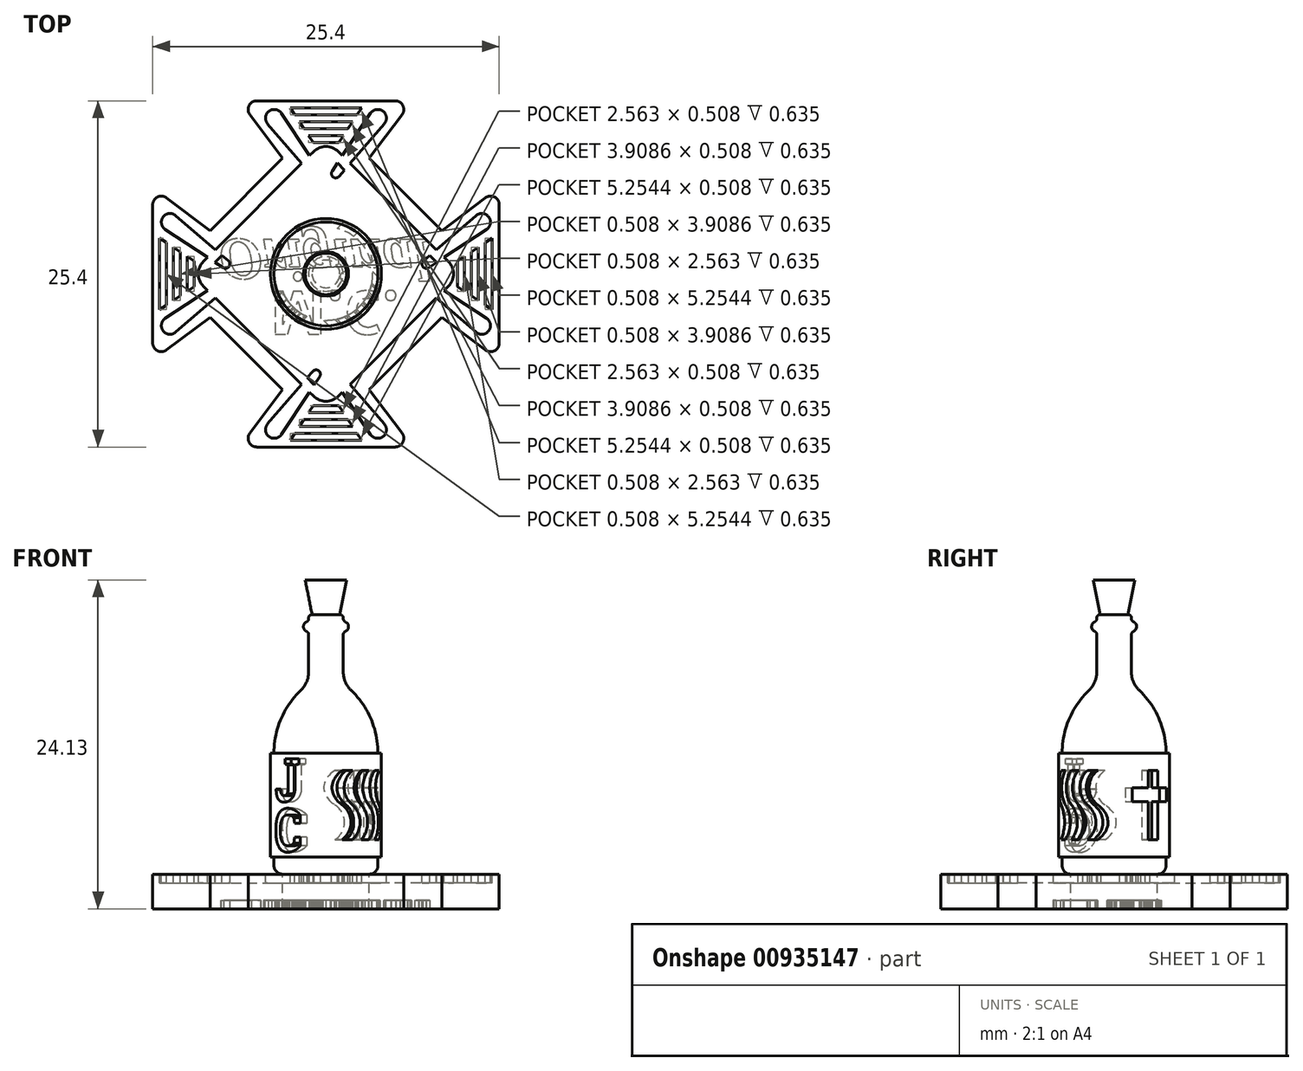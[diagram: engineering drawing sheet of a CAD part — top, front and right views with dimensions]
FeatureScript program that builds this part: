
annotation { "Feature Type Name" : "Feature", "Feature Type Description" : "" }
export const myFeature = defineFeature(function(context is Context, id is Id, definition is map)
    precondition{}
    {
        {
            var Q0;
            Q0=qCreatedBy(makeId("Top.planeOp"),FACE);
            var sketch = newSketch(context, id + "F0", { "sketchPlane" : qUnion([Q0])});
            skLineSegment(sketch, "E0", {"start": v(0, 24.37) * mm, "end": v(0, -22.03) * mm, "construction": true});
            skLineSegment(sketch, "E1", {"start": v(-24.6, 0) * mm, "end": v(22.72, 0) * mm, "construction": true});
            skLineSegment(sketch, "E2", {"start": v(0, 11.67) * mm, "end": v(-11.67, 0) * mm});
            skLineSegment(sketch, "E3.MirrorCS", {"start": v(0, 11.67) * mm, "end": v(11.67, 0) * mm});
            skLineSegment(sketch, "E4.MirrorCS", {"start": v(0, -11.67) * mm, "end": v(-11.67, 0) * mm});
            skLineSegment(sketch, "E5.MirrorCS", {"start": v(0, -11.67) * mm, "end": v(11.67, 0) * mm});
            skLineSegment(sketch, "E6", {"start": v(0, 12.7) * mm, "end": v(-6.35, 12.7) * mm});
            skLineSegment(sketch, "E7", {"start": v(-6.35, 12.7) * mm, "end": v(-3.17, 8.5) * mm});
            skPoint(sketch, "E7.endSnap0", {"position": v(-3.17, 12.7) * mm});
            skLineSegment(sketch, "E8.MirrorCS", {"start": v(0, 12.7) * mm, "end": v(6.35, 12.7) * mm});
            skLineSegment(sketch, "E9.MirrorCS", {"start": v(6.35, 12.7) * mm, "end": v(3.17, 8.5) * mm});
            skLineSegment(sketch, "E10.MirrorCS", {"start": v(6.35, -12.7) * mm, "end": v(3.17, -8.5) * mm});
            skLineSegment(sketch, "E11.MirrorCS", {"start": v(0, -12.7) * mm, "end": v(6.35, -12.7) * mm});
            skLineSegment(sketch, "E12.MirrorCS", {"start": v(0, -12.7) * mm, "end": v(-6.35, -12.7) * mm});
            skLineSegment(sketch, "E13.MirrorCS", {"start": v(-6.35, -12.7) * mm, "end": v(-3.17, -8.5) * mm});
            skLineSegment(sketch, "E14", {"start": v(0, 0) * mm, "end": v(5.84, -5.84) * mm, "construction": true});
            skLineSegment(sketch, "E15.MirrorCS", {"start": v(12.7, -6.35) * mm, "end": v(8.5, -3.18) * mm});
            skLineSegment(sketch, "E16.MirrorCS", {"start": v(12.7, 0) * mm, "end": v(12.7, -6.35) * mm});
            skLineSegment(sketch, "E17.MirrorCS", {"start": v(12.7, 0) * mm, "end": v(12.7, 6.35) * mm});
            skLineSegment(sketch, "E18.MirrorCS", {"start": v(12.7, 6.35) * mm, "end": v(8.5, 3.17) * mm});
            skLineSegment(sketch, "E19.MirrorCS", {"start": v(-12.7, 6.35) * mm, "end": v(-8.5, 3.17) * mm});
            skLineSegment(sketch, "E20.MirrorCS", {"start": v(-12.7, 0) * mm, "end": v(-12.7, 6.35) * mm});
            skLineSegment(sketch, "E21.MirrorCS", {"start": v(-12.7, 0) * mm, "end": v(-12.7, -6.35) * mm});
            skLineSegment(sketch, "E22.MirrorCS", {"start": v(-12.7, -6.35) * mm, "end": v(-8.5, -3.18) * mm});
            skSolve(sketch);
        }
        {
            var Q0;
            Q0=qSketchRegion(id+"F0",true);
            extrude(context, id + "F1", {"entities" : qUnion([Q0]), "oppositeDirection" : true, "depth" : 2.54 * mm, "offsetDistance" : 25.4 * mm});
        }
        {
            var Q0;
            Q0=makeQuery(id+"F1.opExtrude","SWEPT_EDGE",EDGE,{"disambiguationData":[OSD([sQuery(id+"F0.wireOp",EDGE,"E6"),sQuery(id+"F0.wireOp",EDGE,"E7")])]});
            var Q1;
            Q1=makeQuery(id+"F1.opExtrude","SWEPT_EDGE",EDGE,{"disambiguationData":[OSD([sQuery(id+"F0.wireOp",EDGE,"E19.MirrorCS"),sQuery(id+"F0.wireOp",EDGE,"E20.MirrorCS")])]});
            var Q2;
            Q2=makeQuery(id+"F1.opExtrude","SWEPT_EDGE",EDGE,{"disambiguationData":[OSD([sQuery(id+"F0.wireOp",EDGE,"E8.MirrorCS"),sQuery(id+"F0.wireOp",EDGE,"E9.MirrorCS")])]});
            var Q3;
            Q3=makeQuery(id+"F1.opExtrude","SWEPT_EDGE",EDGE,{"disambiguationData":[OSD([sQuery(id+"F0.wireOp",EDGE,"E17.MirrorCS"),sQuery(id+"F0.wireOp",EDGE,"E18.MirrorCS")])]});
            var Q4;
            Q4=makeQuery(id+"F1.opExtrude","SWEPT_EDGE",EDGE,{"disambiguationData":[OSD([sQuery(id+"F0.wireOp",EDGE,"E12.MirrorCS"),sQuery(id+"F0.wireOp",EDGE,"E13.MirrorCS")])]});
            var Q5;
            Q5=makeQuery(id+"F1.opExtrude","SWEPT_EDGE",EDGE,{"disambiguationData":[OSD([sQuery(id+"F0.wireOp",EDGE,"E21.MirrorCS"),sQuery(id+"F0.wireOp",EDGE,"E22.MirrorCS")])]});
            var Q6;
            Q6=makeQuery(id+"F1.opExtrude","SWEPT_EDGE",EDGE,{"disambiguationData":[OSD([sQuery(id+"F0.wireOp",EDGE,"E10.MirrorCS"),sQuery(id+"F0.wireOp",EDGE,"E11.MirrorCS")])]});
            var Q7;
            Q7=makeQuery(id+"F1.opExtrude","SWEPT_EDGE",EDGE,{"disambiguationData":[OSD([sQuery(id+"F0.wireOp",EDGE,"E15.MirrorCS"),sQuery(id+"F0.wireOp",EDGE,"E16.MirrorCS")])]});
            fillet(context, id + "F2", {"entities" : qUnion([Q0, Q1, Q2, Q3, Q4, Q5, Q6, Q7]), "radius" : 0.64 * mm, "tangentPropagation" : true, "allowEdgeOverflow" : false});
        }
        {
            var Q0;
            Q0=makeQuery(id+"F1.opExtrude","CAP_FACE",FACE,{"disambiguationData":[OSD([sQuery(id+"F0.wireOp",EDGE,"E2"),sQuery(id+"F0.wireOp",EDGE,"E3.MirrorCS"),sQuery(id+"F0.wireOp",EDGE,"E4.MirrorCS"),sQuery(id+"F0.wireOp",EDGE,"E5.MirrorCS"),sQuery(id+"F0.wireOp",EDGE,"E6"),sQuery(id+"F0.wireOp",EDGE,"E7"),sQuery(id+"F0.wireOp",EDGE,"E8.MirrorCS"),sQuery(id+"F0.wireOp",EDGE,"E9.MirrorCS"),sQuery(id+"F0.wireOp",EDGE,"E10.MirrorCS"),sQuery(id+"F0.wireOp",EDGE,"E11.MirrorCS"),sQuery(id+"F0.wireOp",EDGE,"E12.MirrorCS"),sQuery(id+"F0.wireOp",EDGE,"E13.MirrorCS"),sQuery(id+"F0.wireOp",EDGE,"E15.MirrorCS"),sQuery(id+"F0.wireOp",EDGE,"E16.MirrorCS"),sQuery(id+"F0.wireOp",EDGE,"E17.MirrorCS"),sQuery(id+"F0.wireOp",EDGE,"E18.MirrorCS"),sQuery(id+"F0.wireOp",EDGE,"E19.MirrorCS"),sQuery(id+"F0.wireOp",EDGE,"E20.MirrorCS"),sQuery(id+"F0.wireOp",EDGE,"E21.MirrorCS"),sQuery(id+"F0.wireOp",EDGE,"E22.MirrorCS")])],"isStart":true});
            var sketch = newSketch(context, id + "F3", { "sketchPlane" : qUnion([Q0])});
            skLineSegment(sketch, "E23", {"start": v(0, 16.4) * mm, "end": v(0, -16.14) * mm, "construction": true});
            skLineSegment(sketch, "E24", {"start": v(-8.98, 0.9) * mm, "end": v(-0.9, 8.98) * mm});
            skArc(sketch, "E25", {"start": v(0, 9.35) * mm, "mid": v(-0.49, 9.26) * mm, "end": v(-0.9, 8.98) * mm});
            skLineSegment(sketch, "E26", {"start": v(0, 0) * mm, "end": v(-13.8, 0) * mm, "construction": true});
            skLineSegment(sketch, "E27", {"start": v(0, 0) * mm, "end": v(-5.84, 5.84) * mm, "construction": true});
            skArc(sketch, "E28.MirrorCS", {"start": v(-9.35, 0) * mm, "mid": v(-9.26, 0.49) * mm, "end": v(-8.98, 0.9) * mm});
            skPoint(sketch, "E29.start.orphan", {"position": v(-9.88, 0) * mm});
            skArc(sketch, "E30.MirrorCS", {"start": v(-9.35, 0) * mm, "mid": v(-9.26, -0.49) * mm, "end": v(-8.98, -0.9) * mm});
            skLineSegment(sketch, "E31.MirrorCS", {"start": v(-8.98, -0.9) * mm, "end": v(-0.9, -8.98) * mm});
            skArc(sketch, "E32.MirrorCS", {"start": v(0, -9.35) * mm, "mid": v(-0.49, -9.26) * mm, "end": v(-0.9, -8.98) * mm});
            skArc(sketch, "E33.MirrorCS", {"start": v(0, 9.35) * mm, "mid": v(0.49, 9.26) * mm, "end": v(0.9, 8.98) * mm});
            skLineSegment(sketch, "E34.MirrorCS", {"start": v(8.98, 0.9) * mm, "end": v(0.9, 8.98) * mm});
            skArc(sketch, "E35.MirrorCS", {"start": v(9.35, 0) * mm, "mid": v(9.26, 0.49) * mm, "end": v(8.98, 0.9) * mm});
            skArc(sketch, "E36.MirrorCS", {"start": v(9.35, 0) * mm, "mid": v(9.26, -0.49) * mm, "end": v(8.98, -0.9) * mm});
            skLineSegment(sketch, "E37.MirrorCS", {"start": v(8.98, -0.9) * mm, "end": v(0.9, -8.98) * mm});
            skArc(sketch, "E38.MirrorCS", {"start": v(0, -9.35) * mm, "mid": v(0.49, -9.26) * mm, "end": v(0.9, -8.98) * mm});
            skLineSegment(sketch, "E39", {"start": v(-2.75, 10.05) * mm, "end": v(2.55, 3.03) * mm, "construction": true});
            skArc(sketch, "E40", {"start": v(-4.18, 11.94) * mm, "mid": v(-4.43, 11.5) * mm, "end": v(-4.28, 11.02) * mm});
            skArc(sketch, "E41", {"start": v(-0.96, 7.15) * mm, "mid": v(-0.76, 7.04) * mm, "end": v(-0.53, 7.1) * mm});
            skLineSegment(sketch, "E42", {"start": v(-4.28, 11.02) * mm, "end": v(-0.96, 7.15) * mm});
            skArc(sketch, "E43.MirrorCS", {"start": v(-0.46, 7.54) * mm, "mid": v(-0.4, 7.3) * mm, "end": v(-0.53, 7.1) * mm});
            skLineSegment(sketch, "E44.MirrorCS", {"start": v(-3.27, 11.78) * mm, "end": v(-0.46, 7.54) * mm});
            skArc(sketch, "E45.MirrorCS", {"start": v(-4.18, 11.94) * mm, "mid": v(-3.7, 12.06) * mm, "end": v(-3.27, 11.78) * mm});
            skArc(sketch, "E46.MirrorCS", {"start": v(4.18, 11.94) * mm, "mid": v(3.7, 12.06) * mm, "end": v(3.27, 11.78) * mm});
            skArc(sketch, "E47.MirrorCS", {"start": v(4.18, 11.94) * mm, "mid": v(4.43, 11.5) * mm, "end": v(4.28, 11.02) * mm});
            skLineSegment(sketch, "E48.MirrorCS", {"start": v(4.28, 11.02) * mm, "end": v(0.96, 7.15) * mm});
            skLineSegment(sketch, "E49.MirrorCS", {"start": v(3.27, 11.78) * mm, "end": v(0.46, 7.54) * mm});
            skArc(sketch, "E50.MirrorCS", {"start": v(0.96, 7.15) * mm, "mid": v(0.76, 7.04) * mm, "end": v(0.53, 7.1) * mm});
            skArc(sketch, "E51.MirrorCS", {"start": v(0.46, 7.54) * mm, "mid": v(0.4, 7.3) * mm, "end": v(0.53, 7.1) * mm});
            skArc(sketch, "E52.MirrorCS", {"start": v(-11.94, 4.18) * mm, "mid": v(-11.5, 4.43) * mm, "end": v(-11.02, 4.28) * mm});
            skArc(sketch, "E53.MirrorCS", {"start": v(-11.94, 4.18) * mm, "mid": v(-12.06, 3.7) * mm, "end": v(-11.78, 3.27) * mm});
            skLineSegment(sketch, "E54.MirrorCS", {"start": v(-11.02, 4.28) * mm, "end": v(-7.15, 0.96) * mm});
            skLineSegment(sketch, "E55.MirrorCS", {"start": v(-11.78, 3.27) * mm, "end": v(-7.54, 0.46) * mm});
            skArc(sketch, "E56.MirrorCS", {"start": v(-7.15, 0.96) * mm, "mid": v(-7.04, 0.76) * mm, "end": v(-7.1, 0.53) * mm});
            skArc(sketch, "E57.MirrorCS", {"start": v(-7.54, 0.46) * mm, "mid": v(-7.3, 0.4) * mm, "end": v(-7.1, 0.53) * mm});
            skArc(sketch, "E58.MirrorCS", {"start": v(-7.15, -0.96) * mm, "mid": v(-7.04, -0.76) * mm, "end": v(-7.1, -0.53) * mm});
            skArc(sketch, "E59.MirrorCS", {"start": v(-7.54, -0.46) * mm, "mid": v(-7.3, -0.4) * mm, "end": v(-7.1, -0.53) * mm});
            skLineSegment(sketch, "E60.MirrorCS", {"start": v(-11.78, -3.27) * mm, "end": v(-7.54, -0.46) * mm});
            skLineSegment(sketch, "E61.MirrorCS", {"start": v(-11.02, -4.28) * mm, "end": v(-7.15, -0.96) * mm});
            skArc(sketch, "E62.MirrorCS", {"start": v(-11.94, -4.18) * mm, "mid": v(-12.06, -3.7) * mm, "end": v(-11.78, -3.27) * mm});
            skArc(sketch, "E63.MirrorCS", {"start": v(-11.94, -4.18) * mm, "mid": v(-11.5, -4.43) * mm, "end": v(-11.02, -4.28) * mm});
            skArc(sketch, "E64.MirrorCS", {"start": v(11.94, 4.18) * mm, "mid": v(11.5, 4.43) * mm, "end": v(11.02, 4.28) * mm});
            skArc(sketch, "E65.MirrorCS", {"start": v(11.94, 4.18) * mm, "mid": v(12.06, 3.7) * mm, "end": v(11.78, 3.27) * mm});
            skLineSegment(sketch, "E66.MirrorCS", {"start": v(11.78, 3.27) * mm, "end": v(7.54, 0.46) * mm});
            skLineSegment(sketch, "E67.MirrorCS", {"start": v(11.02, 4.28) * mm, "end": v(7.15, 0.96) * mm});
            skArc(sketch, "E68.MirrorCS", {"start": v(11.94, -4.18) * mm, "mid": v(12.06, -3.7) * mm, "end": v(11.78, -3.27) * mm});
            skArc(sketch, "E69.MirrorCS", {"start": v(11.94, -4.18) * mm, "mid": v(11.5, -4.43) * mm, "end": v(11.02, -4.28) * mm});
            skLineSegment(sketch, "E70.MirrorCS", {"start": v(11.02, -4.28) * mm, "end": v(7.15, -0.96) * mm});
            skLineSegment(sketch, "E71.MirrorCS", {"start": v(11.78, -3.27) * mm, "end": v(7.54, -0.46) * mm});
            skArc(sketch, "E72.MirrorCS", {"start": v(7.54, -0.46) * mm, "mid": v(7.3, -0.4) * mm, "end": v(7.1, -0.53) * mm});
            skArc(sketch, "E73.MirrorCS", {"start": v(7.15, -0.96) * mm, "mid": v(7.04, -0.76) * mm, "end": v(7.1, -0.53) * mm});
            skArc(sketch, "E74.MirrorCS", {"start": v(7.54, 0.46) * mm, "mid": v(7.3, 0.4) * mm, "end": v(7.1, 0.53) * mm});
            skArc(sketch, "E75.MirrorCS", {"start": v(7.15, 0.96) * mm, "mid": v(7.04, 0.76) * mm, "end": v(7.1, 0.53) * mm});
            skArc(sketch, "E76.MirrorCS", {"start": v(-4.18, -11.94) * mm, "mid": v(-3.7, -12.06) * mm, "end": v(-3.27, -11.78) * mm});
            skArc(sketch, "E77.MirrorCS", {"start": v(-4.18, -11.94) * mm, "mid": v(-4.43, -11.5) * mm, "end": v(-4.28, -11.02) * mm});
            skLineSegment(sketch, "E78.MirrorCS", {"start": v(-4.28, -11.02) * mm, "end": v(-0.96, -7.15) * mm});
            skLineSegment(sketch, "E79.MirrorCS", {"start": v(-3.27, -11.78) * mm, "end": v(-0.46, -7.54) * mm});
            skArc(sketch, "E80.MirrorCS", {"start": v(-0.96, -7.15) * mm, "mid": v(-0.76, -7.04) * mm, "end": v(-0.53, -7.1) * mm});
            skArc(sketch, "E81.MirrorCS", {"start": v(-0.46, -7.54) * mm, "mid": v(-0.4, -7.3) * mm, "end": v(-0.53, -7.1) * mm});
            skArc(sketch, "E82.MirrorCS", {"start": v(0.96, -7.15) * mm, "mid": v(0.76, -7.04) * mm, "end": v(0.53, -7.1) * mm});
            skArc(sketch, "E83.MirrorCS", {"start": v(0.46, -7.54) * mm, "mid": v(0.4, -7.3) * mm, "end": v(0.53, -7.1) * mm});
            skLineSegment(sketch, "E84.MirrorCS", {"start": v(3.27, -11.78) * mm, "end": v(0.46, -7.54) * mm});
            skLineSegment(sketch, "E85.MirrorCS", {"start": v(4.28, -11.02) * mm, "end": v(0.96, -7.15) * mm});
            skArc(sketch, "E86.MirrorCS", {"start": v(4.18, -11.94) * mm, "mid": v(3.7, -12.06) * mm, "end": v(3.27, -11.78) * mm});
            skArc(sketch, "E87.MirrorCS", {"start": v(4.18, -11.94) * mm, "mid": v(4.43, -11.5) * mm, "end": v(4.28, -11.02) * mm});
            skLineSegment(sketch, "E88.0", {"start": v(-8.53, 0.45) * mm, "end": v(-0.45, 8.53) * mm});
            skLineSegment(sketch, "E89.0", {"start": v(8.53, 0.45) * mm, "end": v(0.45, 8.53) * mm});
            skLineSegment(sketch, "E90.0", {"start": v(8.53, -0.45) * mm, "end": v(0.45, -8.53) * mm});
            skLineSegment(sketch, "E91.0", {"start": v(-8.53, -0.45) * mm, "end": v(-0.45, -8.53) * mm});
            skArc(sketch, "E92", {"start": v(0.45, 8.53) * mm, "mid": v(0, 8.72) * mm, "end": v(-0.45, 8.53) * mm});
            skPoint(sketch, "E93.end.orphan", {"position": v(0, 8.98) * mm});
            skPoint(sketch, "E94.MirrorCS.start.orphan", {"position": v(0.45, 8.53) * mm});
            skArc(sketch, "E95.MirrorCS", {"start": v(-8.53, -0.45) * mm, "mid": v(-8.72, 0) * mm, "end": v(-8.53, 0.45) * mm});
            skArc(sketch, "E96.MirrorCS", {"start": v(0.45, -8.53) * mm, "mid": v(0, -8.72) * mm, "end": v(-0.45, -8.53) * mm});
            skArc(sketch, "E97.MirrorCS", {"start": v(8.53, -0.45) * mm, "mid": v(8.72, 0) * mm, "end": v(8.53, 0.45) * mm});
            skSolve(sketch);
        }
        {
            var Q0;
            Q0=qSketchRegion(id+"F3",true);
            var Q1;
            {var subQ0=sQuery(id+"F3.wireOp",EDGE,"E80.MirrorCS");Q1=makeQuery(id+"F3.imprint","IMPRINT",FACE,{"disambiguationData":[TD([[makeQuery(id+"F3.imprint","IMPRINT",EDGE,{"derivedFrom":subQ0}),-1.0]])]});}
            var Q2;
            {var subQ1=sQuery(id+"F3.wireOp",EDGE,"E82.MirrorCS");Q2=makeQuery(id+"F3.imprint","IMPRINT",FACE,{"disambiguationData":[TD([[makeQuery(id+"F3.imprint","IMPRINT",EDGE,{"derivedFrom":subQ1}),1.0]])]});}
            var Q3;
            {var subQ0=sQuery(id+"F3.wireOp",EDGE,"E74.MirrorCS");Q3=makeQuery(id+"F3.imprint","IMPRINT",FACE,{"disambiguationData":[TD([[makeQuery(id+"F3.imprint","IMPRINT",EDGE,{"derivedFrom":subQ0}),-1.0]])]});}
            var Q4;
            {var subQ0=sQuery(id+"F3.wireOp",EDGE,"E50.MirrorCS");Q4=makeQuery(id+"F3.imprint","IMPRINT",FACE,{"disambiguationData":[TD([[makeQuery(id+"F3.imprint","IMPRINT",EDGE,{"derivedFrom":subQ0}),-1.0]])]});}
            var Q5;
            {var subQ1=sQuery(id+"F3.wireOp",EDGE,"E41");Q5=makeQuery(id+"F3.imprint","IMPRINT",FACE,{"disambiguationData":[TD([[makeQuery(id+"F3.imprint","IMPRINT",EDGE,{"derivedFrom":subQ1}),1.0]])]});}
            var Q6;
            {var subQ0=sQuery(id+"F3.wireOp",EDGE,"E56.MirrorCS");Q6=makeQuery(id+"F3.imprint","IMPRINT",FACE,{"disambiguationData":[TD([[makeQuery(id+"F3.imprint","IMPRINT",EDGE,{"derivedFrom":subQ0}),-1.0]])]});}
            var Q7;
            {var subQ4=sQuery(id+"F3.wireOp",EDGE,"E58.MirrorCS");Q7=makeQuery(id+"F3.imprint","IMPRINT",FACE,{"disambiguationData":[TD([[makeQuery(id+"F3.imprint","IMPRINT",EDGE,{"derivedFrom":subQ4}),1.0]])]});}
            var Q8;
            {var subQ0=sQuery(id+"F3.wireOp",EDGE,"E72.MirrorCS");Q8=makeQuery(id+"F3.imprint","IMPRINT",FACE,{"disambiguationData":[TD([[makeQuery(id+"F3.imprint","IMPRINT",EDGE,{"derivedFrom":subQ0}),1.0]])]});}
            extrude(context, id + "F4", {"entities" : qUnion([Q0, Q1, Q2, Q3, Q4, Q5, Q6, Q7, Q8]), "operationType" : NewBodyOperationType.REMOVE, "oppositeDirection" : true, "depth" : 0.64 * mm, "offsetDistance" : 25.4 * mm});
        }
        {
            var Q0;
            {var subQ29=sQuery(id+"F0.wireOp",EDGE,"E22.MirrorCS");var subQ30=sQuery(id+"F0.wireOp",EDGE,"E21.MirrorCS");var subQ31=sQuery(id+"F0.wireOp",EDGE,"E17.MirrorCS");var subQ32=sQuery(id+"F0.wireOp",EDGE,"E16.MirrorCS");var subQ33=sQuery(id+"F0.wireOp",EDGE,"E20.MirrorCS");var subQ34=sQuery(id+"F0.wireOp",EDGE,"E19.MirrorCS");var subQ35=sQuery(id+"F0.wireOp",EDGE,"E15.MirrorCS");var subQ37=sQuery(id+"F0.wireOp",EDGE,"E12.MirrorCS");var subQ38=sQuery(id+"F0.wireOp",EDGE,"E11.MirrorCS");var subQ39=sQuery(id+"F0.wireOp",EDGE,"E9.MirrorCS");var subQ40=sQuery(id+"F0.wireOp",EDGE,"E8.MirrorCS");var subQ41=sQuery(id+"F0.wireOp",EDGE,"E7");var subQ44=sQuery(id+"F0.wireOp",EDGE,"E10.MirrorCS");var subQ45=sQuery(id+"F0.wireOp",EDGE,"E13.MirrorCS");var subQ46=sQuery(id+"F0.wireOp",EDGE,"E6");var subQ52=sQuery(id+"F0.wireOp",EDGE,"E18.MirrorCS");var subQ53=sQuery(id+"F0.wireOp",EDGE,"E2");var subQ58=sQuery(id+"F0.wireOp",EDGE,"E5.MirrorCS");var subQ59=sQuery(id+"F0.wireOp",EDGE,"E3.MirrorCS");var subQ60=sQuery(id+"F0.wireOp",EDGE,"E4.MirrorCS");Q0=makeQuery(id+"F4.boolean.opBoolean","SPLIT",FACE,{"disambiguationData":[TD([makeQuery(id+"F1.opExtrude","SWEPT_FACE",FACE,{"disambiguationData":[OSD([subQ53])]})])],"derivedFrom":makeQuery(id+"F1.opExtrude","CAP_FACE",FACE,{"disambiguationData":[OSD([subQ53,subQ59,subQ60,subQ58,subQ46,subQ41,subQ40,subQ39,subQ44,subQ38,subQ37,subQ45,subQ35,subQ32,subQ31,subQ52,subQ34,subQ33,subQ30,subQ29])],"isStart":true})});}
            var sketch = newSketch(context, id + "F5", { "sketchPlane" : qUnion([Q0])});
            skLineSegment(sketch, "E98", {"start": v(0, 15.67) * mm, "end": v(0, -18.97) * mm, "construction": true});
            skLineSegment(sketch, "E99", {"start": v(-16.91, 0) * mm, "end": v(16.57, 0) * mm, "construction": true});
            skLineSegment(sketch, "E100", {"start": v(-12.2, 2.63) * mm, "end": v(-12.2, 0) * mm});
            skLineSegment(sketch, "E101", {"start": v(-12.2, 2.63) * mm, "end": v(-8.22, 0) * mm, "construction": true});
            skLineSegment(sketch, "E102", {"start": v(-11.18, 1.95) * mm, "end": v(-11.18, 0) * mm});
            skLineSegment(sketch, "E103", {"start": v(-10.16, 1.28) * mm, "end": v(-10.16, 0) * mm});
            skLineSegment(sketch, "E104.0", {"start": v(-11.68, 2.3) * mm, "end": v(-11.68, 0) * mm});
            skLineSegment(sketch, "E105.0", {"start": v(-10.67, 1.62) * mm, "end": v(-10.67, 0) * mm});
            skLineSegment(sketch, "E106.0", {"start": v(-9.65, 0.95) * mm, "end": v(-9.65, 0) * mm});
            skLineSegment(sketch, "E107", {"start": v(-12.2, 2.63) * mm, "end": v(-11.68, 2.3) * mm});
            skLineSegment(sketch, "E108", {"start": v(-11.18, 1.95) * mm, "end": v(-10.67, 1.62) * mm});
            skLineSegment(sketch, "E109", {"start": v(-10.16, 1.28) * mm, "end": v(-9.65, 0.95) * mm});
            skLineSegment(sketch, "E110.MirrorCS", {"start": v(-12.2, -2.63) * mm, "end": v(-12.2, 0) * mm});
            skLineSegment(sketch, "E111.MirrorCS", {"start": v(-11.68, -2.3) * mm, "end": v(-11.68, 0) * mm});
            skLineSegment(sketch, "E112.MirrorCS", {"start": v(-11.18, -1.95) * mm, "end": v(-11.18, 0) * mm});
            skLineSegment(sketch, "E113.MirrorCS", {"start": v(-10.67, -1.62) * mm, "end": v(-10.67, 0) * mm});
            skLineSegment(sketch, "E114.MirrorCS", {"start": v(-10.16, -1.28) * mm, "end": v(-10.16, 0) * mm});
            skLineSegment(sketch, "E115.MirrorCS", {"start": v(-9.65, -0.95) * mm, "end": v(-9.65, 0) * mm});
            skLineSegment(sketch, "E116.MirrorCS", {"start": v(-10.16, -1.28) * mm, "end": v(-9.65, -0.95) * mm});
            skLineSegment(sketch, "E117.MirrorCS", {"start": v(-11.18, -1.95) * mm, "end": v(-10.67, -1.62) * mm});
            skLineSegment(sketch, "E118.MirrorCS", {"start": v(-12.2, -2.63) * mm, "end": v(-11.68, -2.3) * mm});
            skLineSegment(sketch, "E119.MirrorCS", {"start": v(12.2, 2.63) * mm, "end": v(11.68, 2.3) * mm});
            skLineSegment(sketch, "E120.MirrorCS", {"start": v(11.18, 1.95) * mm, "end": v(10.67, 1.62) * mm});
            skLineSegment(sketch, "E121.MirrorCS", {"start": v(10.16, 1.28) * mm, "end": v(9.65, 0.95) * mm});
            skLineSegment(sketch, "E122.MirrorCS", {"start": v(10.16, -1.28) * mm, "end": v(9.65, -0.95) * mm});
            skLineSegment(sketch, "E123.MirrorCS", {"start": v(11.18, -1.95) * mm, "end": v(10.67, -1.62) * mm});
            skLineSegment(sketch, "E124.MirrorCS", {"start": v(12.2, -2.63) * mm, "end": v(11.68, -2.3) * mm});
            skLineSegment(sketch, "E125.MirrorCS", {"start": v(12.2, -2.63) * mm, "end": v(12.2, 0) * mm});
            skLineSegment(sketch, "E126.MirrorCS", {"start": v(11.68, -2.3) * mm, "end": v(11.68, 0) * mm});
            skLineSegment(sketch, "E127.MirrorCS", {"start": v(11.18, -1.95) * mm, "end": v(11.18, 0) * mm});
            skLineSegment(sketch, "E128.MirrorCS", {"start": v(10.67, -1.62) * mm, "end": v(10.67, 0) * mm});
            skLineSegment(sketch, "E129.MirrorCS", {"start": v(10.16, -1.28) * mm, "end": v(10.16, 0) * mm});
            skLineSegment(sketch, "E130.MirrorCS", {"start": v(9.65, -0.95) * mm, "end": v(9.65, 0) * mm});
            skLineSegment(sketch, "E131.MirrorCS", {"start": v(9.65, 0.95) * mm, "end": v(9.65, 0) * mm});
            skLineSegment(sketch, "E132.MirrorCS", {"start": v(10.16, 1.28) * mm, "end": v(10.16, 0) * mm});
            skLineSegment(sketch, "E133.MirrorCS", {"start": v(10.67, 1.62) * mm, "end": v(10.67, 0) * mm});
            skLineSegment(sketch, "E134.MirrorCS", {"start": v(11.18, 1.95) * mm, "end": v(11.18, 0) * mm});
            skLineSegment(sketch, "E135.MirrorCS", {"start": v(11.68, 2.3) * mm, "end": v(11.68, 0) * mm});
            skLineSegment(sketch, "E136.MirrorCS", {"start": v(12.2, 2.63) * mm, "end": v(12.2, 0) * mm});
            skLineSegment(sketch, "E137", {"start": v(0, 0) * mm, "end": v(-5.84, 5.84) * mm, "construction": true});
            skLineSegment(sketch, "E138.MirrorCS", {"start": v(-2.63, 12.2) * mm, "end": v(-2.3, 11.68) * mm});
            skLineSegment(sketch, "E139.MirrorCS", {"start": v(-1.95, 11.18) * mm, "end": v(-1.62, 10.67) * mm});
            skLineSegment(sketch, "E140.MirrorCS", {"start": v(-1.28, 10.16) * mm, "end": v(-0.95, 9.65) * mm});
            skLineSegment(sketch, "E141.MirrorCS", {"start": v(1.28, 10.16) * mm, "end": v(0.95, 9.65) * mm});
            skLineSegment(sketch, "E142.MirrorCS", {"start": v(1.95, 11.18) * mm, "end": v(1.62, 10.67) * mm});
            skLineSegment(sketch, "E143.MirrorCS", {"start": v(2.63, 12.2) * mm, "end": v(2.3, 11.68) * mm});
            skLineSegment(sketch, "E144.MirrorCS", {"start": v(2.63, 12.2) * mm, "end": v(0, 12.2) * mm});
            skLineSegment(sketch, "E145.MirrorCS", {"start": v(2.3, 11.68) * mm, "end": v(0, 11.68) * mm});
            skLineSegment(sketch, "E146.MirrorCS", {"start": v(1.95, 11.18) * mm, "end": v(0, 11.18) * mm});
            skLineSegment(sketch, "E147.MirrorCS", {"start": v(1.62, 10.67) * mm, "end": v(0, 10.67) * mm});
            skLineSegment(sketch, "E148.MirrorCS", {"start": v(1.28, 10.16) * mm, "end": v(0, 10.16) * mm});
            skLineSegment(sketch, "E149.MirrorCS", {"start": v(0.95, 9.65) * mm, "end": v(0, 9.65) * mm});
            skLineSegment(sketch, "E150.MirrorCS", {"start": v(-0.95, 9.65) * mm, "end": v(0, 9.65) * mm});
            skLineSegment(sketch, "E151.MirrorCS", {"start": v(-1.28, 10.16) * mm, "end": v(0, 10.16) * mm});
            skLineSegment(sketch, "E152.MirrorCS", {"start": v(-1.62, 10.67) * mm, "end": v(0, 10.67) * mm});
            skLineSegment(sketch, "E153.MirrorCS", {"start": v(-1.95, 11.18) * mm, "end": v(0, 11.18) * mm});
            skLineSegment(sketch, "E154.MirrorCS", {"start": v(-2.3, 11.68) * mm, "end": v(0, 11.68) * mm});
            skLineSegment(sketch, "E155.MirrorCS", {"start": v(-2.63, 12.2) * mm, "end": v(0, 12.2) * mm});
            skLineSegment(sketch, "E156.MirrorCS", {"start": v(2.63, -12.2) * mm, "end": v(2.3, -11.68) * mm});
            skLineSegment(sketch, "E157.MirrorCS", {"start": v(1.95, -11.18) * mm, "end": v(1.62, -10.67) * mm});
            skLineSegment(sketch, "E158.MirrorCS", {"start": v(1.28, -10.16) * mm, "end": v(0.95, -9.65) * mm});
            skLineSegment(sketch, "E159.MirrorCS", {"start": v(-1.28, -10.16) * mm, "end": v(-0.95, -9.65) * mm});
            skLineSegment(sketch, "E160.MirrorCS", {"start": v(-1.95, -11.18) * mm, "end": v(-1.62, -10.67) * mm});
            skLineSegment(sketch, "E161.MirrorCS", {"start": v(-2.63, -12.2) * mm, "end": v(-2.3, -11.68) * mm});
            skLineSegment(sketch, "E162.MirrorCS", {"start": v(-2.63, -12.2) * mm, "end": v(0, -12.2) * mm});
            skLineSegment(sketch, "E163.MirrorCS", {"start": v(-2.3, -11.68) * mm, "end": v(0, -11.68) * mm});
            skLineSegment(sketch, "E164.MirrorCS", {"start": v(2.3, -11.68) * mm, "end": v(0, -11.68) * mm});
            skLineSegment(sketch, "E165.MirrorCS", {"start": v(2.63, -12.2) * mm, "end": v(0, -12.2) * mm});
            skLineSegment(sketch, "E166.MirrorCS", {"start": v(1.95, -11.18) * mm, "end": v(0, -11.18) * mm});
            skLineSegment(sketch, "E167.MirrorCS", {"start": v(-1.95, -11.18) * mm, "end": v(0, -11.18) * mm});
            skLineSegment(sketch, "E168.MirrorCS", {"start": v(-1.62, -10.67) * mm, "end": v(0, -10.67) * mm});
            skLineSegment(sketch, "E169.MirrorCS", {"start": v(1.62, -10.67) * mm, "end": v(0, -10.67) * mm});
            skLineSegment(sketch, "E170.MirrorCS", {"start": v(1.28, -10.16) * mm, "end": v(0, -10.16) * mm});
            skLineSegment(sketch, "E171.MirrorCS", {"start": v(-1.28, -10.16) * mm, "end": v(0, -10.16) * mm});
            skLineSegment(sketch, "E172.MirrorCS", {"start": v(-0.95, -9.65) * mm, "end": v(0, -9.65) * mm});
            skLineSegment(sketch, "E173.MirrorCS", {"start": v(0.95, -9.65) * mm, "end": v(0, -9.65) * mm});
            skSolve(sketch);
        }
        {
            var Q0;
            Q0=qSketchRegion(id+"F5",true);
            extrude(context, id + "F6", {"entities" : qUnion([Q0]), "operationType" : NewBodyOperationType.REMOVE, "oppositeDirection" : true, "depth" : 0.64 * mm, "offsetDistance" : 25.4 * mm});
        }
        {
            var Q0;
            Q0=makeQuery(id+"F1.opExtrude","CAP_FACE",FACE,{"disambiguationData":[OSD([sQuery(id+"F0.wireOp",EDGE,"E2"),sQuery(id+"F0.wireOp",EDGE,"E3.MirrorCS"),sQuery(id+"F0.wireOp",EDGE,"E4.MirrorCS"),sQuery(id+"F0.wireOp",EDGE,"E5.MirrorCS"),sQuery(id+"F0.wireOp",EDGE,"E6"),sQuery(id+"F0.wireOp",EDGE,"E7"),sQuery(id+"F0.wireOp",EDGE,"E8.MirrorCS"),sQuery(id+"F0.wireOp",EDGE,"E9.MirrorCS"),sQuery(id+"F0.wireOp",EDGE,"E10.MirrorCS"),sQuery(id+"F0.wireOp",EDGE,"E11.MirrorCS"),sQuery(id+"F0.wireOp",EDGE,"E12.MirrorCS"),sQuery(id+"F0.wireOp",EDGE,"E13.MirrorCS"),sQuery(id+"F0.wireOp",EDGE,"E15.MirrorCS"),sQuery(id+"F0.wireOp",EDGE,"E16.MirrorCS"),sQuery(id+"F0.wireOp",EDGE,"E17.MirrorCS"),sQuery(id+"F0.wireOp",EDGE,"E18.MirrorCS"),sQuery(id+"F0.wireOp",EDGE,"E19.MirrorCS"),sQuery(id+"F0.wireOp",EDGE,"E20.MirrorCS"),sQuery(id+"F0.wireOp",EDGE,"E21.MirrorCS"),sQuery(id+"F0.wireOp",EDGE,"E22.MirrorCS")])],"isStart":false});
            var sketch = newSketch(context, id + "F7", { "sketchPlane" : qUnion([Q0])});
            skText(sketch, "E174", { "text": "Original", "fontName": "Tinos-BoldItalic.ttf"});
            skLineSegment(sketch, "E175", {"start": v(0, 12.7) * mm, "end": v(0, -12.7) * mm});
            skText(sketch, "E176", { "text": "M.C.", "fontName": "OpenSans-Bold.ttf"});
            const initialGuessF7  = {"E174": [-0.00785, -0.00254, 1, 0, 0.00318], "E176": [-0.00412, 0.00127, 1, 0, 0.00318]};
            skSetInitialGuess(sketch, initialGuessF7);
            skSolve(sketch);
        }
        {
            var Q0;
            Q0=qSketchRegion(id+"F7",true);
            extrude(context, id + "F8", {"entities" : qUnion([Q0]), "operationType" : NewBodyOperationType.REMOVE, "oppositeDirection" : true, "depth" : 0.64 * mm, "offsetDistance" : 25.4 * mm});
        }
        {
            var Q0;
            Q0=qCreatedBy(makeId("Front.planeOp"),FACE);
            var sketch = newSketch(context, id + "F9", { "sketchPlane" : qUnion([Q0])});
            skLineSegment(sketch, "E177", {"start": v(0, 0) * mm, "end": v(0, 19.05) * mm});
            skLineSegment(sketch, "E178", {"start": v(0, 0) * mm, "end": v(-3.17, 0) * mm});
            skLineSegment(sketch, "E179", {"start": v(-3.81, 0.64) * mm, "end": v(-3.81, 8.9) * mm});
            skLineSegment(sketch, "E180", {"start": v(-1.27, 14.85) * mm, "end": v(-1.27, 19.05) * mm});
            skLineSegment(sketch, "E181", {"start": v(-1.27, 19.05) * mm, "end": v(0, 19.05) * mm});
            skArc(sketch, "E182", {"start": v(-1.86, 13.47) * mm, "mid": v(-3.3, 11.38) * mm, "end": v(-3.81, 8.9) * mm});
            skPoint(sketch, "E182.centerSnap0", {"position": v(-2.54, 8.9) * mm});
            skArc(sketch, "E183", {"start": v(-1.86, 13.47) * mm, "mid": v(-1.42, 14.1) * mm, "end": v(-1.27, 14.85) * mm});
            skPoint(sketch, "E184.orphan", {"position": v(-1.27, 8.9) * mm});
            skArc(sketch, "E185", {"start": v(-3.81, 0.63) * mm, "mid": v(-3.62, 0.19) * mm, "end": v(-3.18, 0) * mm});
            skLineSegment(sketch, "E186", {"start": v(-1.02, 19.05) * mm, "end": v(-1.52, 21.59) * mm});
            skLineSegment(sketch, "E187", {"start": v(-1.52, 21.59) * mm, "end": v(0, 21.59) * mm});
            skLineSegment(sketch, "E188", {"start": v(0, 21.59) * mm, "end": v(0, 19.05) * mm});
            skSolve(sketch);
        }
        {
            var Q0;
            Q0 = qSketchRegion(id + "F9", true);
            var Q1;
            Q1=sQuery(id+"F9.wireOp",EDGE,"E177");
            revolve(context, id + "F10", {"operationType" : NewBodyOperationType.ADD, "surfaceOperationType" : NewSurfaceOperationType.NEW, "entities" : qUnion([Q0]), "axis" : qUnion([Q1]), "revolveType" : RevolveType.FULL});
        }
        {
            var Q0;
            Q0=makeQuery(id+"F1.opExtrude","SWEPT_FACE",FACE,{"disambiguationData":[OSD([sQuery(id+"F0.wireOp",EDGE,"E4.MirrorCS")])]});
            cPlane(context, id + "F11", {"entities" : qUnion([Q0]), "cplaneType" : CPlaneType.OFFSET, "offset" : 8.25 * mm, "oppositeDirection" : true, "width" : 152.4 * mm, "height" : 152.4 * mm});
        }
        {
            var Q0;
            Q0=qCreatedBy(id+"F11.planeOp",FACE);
            var sketch = newSketch(context, id + "F12", { "sketchPlane" : qUnion([Q0])});
            skLineSegment(sketch, "E189", {"start": v(3.8, 8.9) * mm, "end": v(3.8, 1.27) * mm});
            skLineSegment(sketch, "E190", {"start": v(4.06, 1.27) * mm, "end": v(4.06, 8.9) * mm});
            skLineSegment(sketch, "E191", {"start": v(4.06, 8.9) * mm, "end": v(4.06, 8.9) * mm});
            skLineSegment(sketch, "E192", {"start": v(3.8, 8.9) * mm, "end": v(4.06, 8.9) * mm});
            skLineSegment(sketch, "E193", {"start": v(0, 0) * mm, "end": v(0, 11.14) * mm, "construction": true});
            skLineSegment(sketch, "E194.MirrorCS", {"start": v(-3.8, 8.9) * mm, "end": v(-4.06, 8.9) * mm});
            skLineSegment(sketch, "E195.MirrorCS", {"start": v(-3.8, 8.9) * mm, "end": v(-3.8, 1.27) * mm});
            skLineSegment(sketch, "E196.MirrorCS", {"start": v(-4.06, 1.27) * mm, "end": v(-4.06, 8.9) * mm});
            skLineSegment(sketch, "E197", {"start": v(-4.06, 1.27) * mm, "end": v(-3.8, 1.27) * mm});
            skLineSegment(sketch, "E198.trimOffspring", {"start": v(3.81, 1.27) * mm, "end": v(4.06, 1.27) * mm});
            skPoint(sketch, "E199.orphan", {"position": v(-3.8, 0.63) * mm});
            skPoint(sketch, "E200.orphan", {"position": v(-4.06, 0.63) * mm});
            skPoint(sketch, "E201.start.orphan", {"position": v(3.8, 0.63) * mm});
            skPoint(sketch, "E202.orphan", {"position": v(4.06, 0.63) * mm});
            skSolve(sketch);
        }
        {
            var Q0;
            Q0=makeQuery(id+"F12.imprint","IMPRINT",FACE,{"disambiguationData":[TD([[makeQuery(id+"F12.imprint","IMPRINT",EDGE,{"derivedFrom":sQuery(id+"F12.wireOp",EDGE,"E189")}),1.0]])]});
            var Q1;
            Q1=sQuery(id+"F12.wireOp",EDGE,"E193");
            revolve(context, id + "F13", {"operationType" : NewBodyOperationType.ADD, "surfaceOperationType" : NewSurfaceOperationType.NEW, "entities" : qUnion([Q0]), "axis" : qUnion([Q1]), "revolveType" : RevolveType.FULL, "oppositeDirection" : true});
        }
        {
            var Q0;
            Q0=makeQuery(id+"F1.opExtrude","SWEPT_FACE",FACE,{"disambiguationData":[OSD([sQuery(id+"F0.wireOp",EDGE,"E4.MirrorCS")])]});
            cPlane(context, id + "F14", {"entities" : qUnion([Q0]), "cplaneType" : CPlaneType.OFFSET, "offset" : 4.2 * mm, "oppositeDirection" : true, "width" : 152.4 * mm, "height" : 152.4 * mm});
        }
        {
            var Q0;
            Q0=qCreatedBy(id+"F14.planeOp",FACE);
            var sketch = newSketch(context, id + "F15", { "sketchPlane" : qUnion([Q0])});
            skText(sketch, "E203", { "text": "J", "fontName": "RobotoSlab-Bold.ttf"});
            skText(sketch, "E204", { "text": "C", "fontName": "RobotoSlab-Bold.ttf"});
            skLineSegment(sketch, "E205", {"start": v(0, 0) * mm, "end": v(0, 17.51) * mm, "construction": true});
            const initialGuessF15  = {"E203": [-0.00139, 0.00533, 1, 0, 0.00317], "E204": [-0.00148, 0.00165, 1, 0, 0.00318]};
            skSetInitialGuess(sketch, initialGuessF15);
            skSolve(sketch);
        }
        {
            var Q0;
            Q0 = qSketchRegion(id + "F15", true);
            extrude(context, id + "F16", {"entities" : qUnion([Q0]), "operationType" : NewBodyOperationType.REMOVE, "oppositeDirection" : true, "depth" : 2.54 * mm, "offsetDistance" : 25.4 * mm});
        }
        {
            var Q0;
            Q0=qCreatedBy(id+"F11.planeOp",FACE);
            var sketch = newSketch(context, id + "F17", { "sketchPlane" : qUnion([Q0])});
            skLineSegment(sketch, "E206", {"start": v(0, 1.02) * mm, "end": v(0, 8.9) * mm});
            skLineSegment(sketch, "E207", {"start": v(0, 8.9) * mm, "end": v(3.43, 8.9) * mm});
            skLineSegment(sketch, "E208", {"start": v(3.43, 8.9) * mm, "end": v(3.43, 1.02) * mm});
            skLineSegment(sketch, "E209", {"start": v(0, 1.02) * mm, "end": v(3.43, 1.02) * mm});
            skSolve(sketch);
        }
        {
            var Q0;
            Q0=makeQuery(id+"F1.opExtrude","SWEPT_FACE",FACE,{"disambiguationData":[OSD([sQuery(id+"F0.wireOp",EDGE,"E5.MirrorCS")])]});
            var sketch = newSketch(context, id + "F18", { "sketchPlane" : qUnion([Q0])});
            skLineSegment(sketch, "E210", {"start": v(0, 0) * mm, "end": v(0, 8.9) * mm, "construction": true});
            skArc(sketch, "E211", {"start": v(0, 7.62) * mm, "mid": v(-0.63, 6.35) * mm, "end": v(0, 5.08) * mm, "construction": true});
            skArc(sketch, "E212", {"start": v(0, 2.54) * mm, "mid": v(0.64, 3.81) * mm, "end": v(0, 5.08) * mm, "construction": true});
            skLineSegment(sketch, "E213", {"start": v(-0.95, 3.81) * mm, "end": v(0.95, 6.35) * mm, "construction": true});
            skPoint(sketch, "E214", {"position": v(0, 5.08) * mm});
            skLineSegment(sketch, "E215", {"start": v(0, 2.54) * mm, "end": v(3.7, 2.54) * mm, "construction": true});
            skLineSegment(sketch, "E216", {"start": v(0, 2.54) * mm, "end": v(-3.97, 2.54) * mm, "construction": true});
            skLineSegment(sketch, "E217", {"start": v(0, 7.62) * mm, "end": v(-3.66, 7.62) * mm, "construction": true});
            skLineSegment(sketch, "E218", {"start": v(0, 7.62) * mm, "end": v(4.02, 7.62) * mm, "construction": true});
            skArc(sketch, "E219.1.0.0", {"start": v(0.38, 7.62) * mm, "mid": v(-0.25, 6.35) * mm, "end": v(0.38, 5.08) * mm});
            skArc(sketch, "E219.1.0.1", {"start": v(0.38, 2.54) * mm, "mid": v(1.02, 3.81) * mm, "end": v(0.38, 5.08) * mm});
            skArc(sketch, "E219.2.0.0", {"start": v(0.76, 7.62) * mm, "mid": v(0.13, 6.35) * mm, "end": v(0.76, 5.08) * mm, "construction": true});
            skArc(sketch, "E219.2.0.1", {"start": v(0.76, 2.54) * mm, "mid": v(1.4, 3.81) * mm, "end": v(0.76, 5.08) * mm, "construction": true});
            skArc(sketch, "E219.3.0.0", {"start": v(1.14, 7.62) * mm, "mid": v(0.5, 6.35) * mm, "end": v(1.14, 5.08) * mm});
            skArc(sketch, "E219.3.0.1", {"start": v(1.14, 2.54) * mm, "mid": v(1.78, 3.81) * mm, "end": v(1.14, 5.08) * mm});
            skArc(sketch, "E219.4.0.0", {"start": v(1.52, 7.62) * mm, "mid": v(0.89, 6.35) * mm, "end": v(1.52, 5.08) * mm, "construction": true});
            skArc(sketch, "E219.4.0.1", {"start": v(1.52, 2.54) * mm, "mid": v(2.16, 3.81) * mm, "end": v(1.52, 5.08) * mm, "construction": true});
            skArc(sketch, "E219.5.0.0", {"start": v(1.9, 7.62) * mm, "mid": v(1.27, 6.35) * mm, "end": v(1.9, 5.08) * mm});
            skArc(sketch, "E219.5.0.1", {"start": v(1.9, 2.54) * mm, "mid": v(2.54, 3.81) * mm, "end": v(1.9, 5.08) * mm});
            skLineSegment(sketch, "E219.direction1", {"start": v(0, 5.08) * mm, "end": v(0.38, 5.08) * mm, "construction": true});
            skArc(sketch, "E220.1.0.0", {"start": v(-0.38, 7.62) * mm, "mid": v(-1.02, 6.35) * mm, "end": v(-0.38, 5.08) * mm});
            skArc(sketch, "E220.1.0.1", {"start": v(-0.38, 2.54) * mm, "mid": v(0.25, 3.81) * mm, "end": v(-0.38, 5.08) * mm});
            skArc(sketch, "E220.2.0.0", {"start": v(-0.76, 7.62) * mm, "mid": v(-1.4, 6.35) * mm, "end": v(-0.76, 5.08) * mm, "construction": true});
            skArc(sketch, "E220.2.0.1", {"start": v(-0.76, 2.54) * mm, "mid": v(-0.13, 3.81) * mm, "end": v(-0.76, 5.08) * mm, "construction": true});
            skArc(sketch, "E220.3.0.0", {"start": v(-1.14, 7.62) * mm, "mid": v(-1.78, 6.35) * mm, "end": v(-1.14, 5.08) * mm});
            skArc(sketch, "E220.3.0.1", {"start": v(-1.14, 2.54) * mm, "mid": v(-0.5, 3.81) * mm, "end": v(-1.14, 5.08) * mm});
            skArc(sketch, "E220.4.0.0", {"start": v(-1.52, 7.62) * mm, "mid": v(-2.16, 6.35) * mm, "end": v(-1.52, 5.08) * mm, "construction": true});
            skArc(sketch, "E220.4.0.1", {"start": v(-1.52, 2.54) * mm, "mid": v(-0.89, 3.81) * mm, "end": v(-1.52, 5.08) * mm, "construction": true});
            skArc(sketch, "E220.5.0.0", {"start": v(-1.9, 7.62) * mm, "mid": v(-2.54, 6.35) * mm, "end": v(-1.9, 5.08) * mm});
            skArc(sketch, "E220.5.0.1", {"start": v(-1.9, 2.54) * mm, "mid": v(-1.27, 3.81) * mm, "end": v(-1.9, 5.08) * mm});
            skLineSegment(sketch, "E220.direction1", {"start": v(0, 5.08) * mm, "end": v(-0.38, 5.08) * mm, "construction": true});
            skLineSegment(sketch, "E221", {"start": v(-1.9, 7.62) * mm, "end": v(-1.14, 7.62) * mm});
            skLineSegment(sketch, "E222", {"start": v(-1.9, 2.54) * mm, "end": v(-1.14, 2.54) * mm});
            skLineSegment(sketch, "E223.trimOffspring", {"start": v(-0.38, 7.62) * mm, "end": v(0.38, 7.62) * mm});
            skLineSegment(sketch, "E224.trimOffspring", {"start": v(1.14, 7.62) * mm, "end": v(1.9, 7.62) * mm});
            skLineSegment(sketch, "E225.trimOffspring", {"start": v(-0.38, 2.54) * mm, "end": v(0.38, 2.54) * mm});
            skLineSegment(sketch, "E226.trimOffspring", {"start": v(1.14, 2.54) * mm, "end": v(1.9, 2.54) * mm});
            skSolve(sketch);
        }
        {
            var Q0;
            Q0 = qSketchRegion(id + "F18", true);
            extrude(context, id + "F19", {"entities" : qUnion([Q0]), "operationType" : NewBodyOperationType.REMOVE, "oppositeDirection" : true, "depth" : 7.62 * mm, "offsetDistance" : 25.4 * mm});
        }
        {
            var Q0;
            Q0=makeQuery(id+"F1.opExtrude","SWEPT_FACE",FACE,{"disambiguationData":[OSD([sQuery(id+"F0.wireOp",EDGE,"E3.MirrorCS")])]});
            var sketch = newSketch(context, id + "F20", { "sketchPlane" : qUnion([Q0])});
            skLineSegment(sketch, "E227", {"start": v(0, 0) * mm, "end": v(0, 9.18) * mm, "construction": true});
            skLineSegment(sketch, "E228", {"start": v(0, 7.62) * mm, "end": v(-0.5, 7.62) * mm});
            skLineSegment(sketch, "E229", {"start": v(-0.5, 7.62) * mm, "end": v(-0.5, 6.35) * mm});
            skLineSegment(sketch, "E230", {"start": v(-0.5, 6.35) * mm, "end": v(-1.78, 6.35) * mm});
            skLineSegment(sketch, "E231", {"start": v(-1.78, 6.35) * mm, "end": v(-1.78, 5.33) * mm});
            skLineSegment(sketch, "E232", {"start": v(-1.78, 5.33) * mm, "end": v(-0.5, 5.33) * mm});
            skLineSegment(sketch, "E233", {"start": v(-0.5, 5.33) * mm, "end": v(-0.5, 2.54) * mm});
            skLineSegment(sketch, "E234", {"start": v(-0.5, 2.54) * mm, "end": v(0, 2.54) * mm});
            skLineSegment(sketch, "E235.MirrorCS", {"start": v(0, 7.62) * mm, "end": v(0.5, 7.62) * mm});
            skLineSegment(sketch, "E236.MirrorCS", {"start": v(0.5, 7.62) * mm, "end": v(0.5, 6.35) * mm});
            skLineSegment(sketch, "E237.MirrorCS", {"start": v(0.5, 6.35) * mm, "end": v(1.78, 6.35) * mm});
            skLineSegment(sketch, "E238.MirrorCS", {"start": v(1.78, 6.35) * mm, "end": v(1.78, 5.33) * mm});
            skLineSegment(sketch, "E239.MirrorCS", {"start": v(1.78, 5.33) * mm, "end": v(0.5, 5.33) * mm});
            skLineSegment(sketch, "E240.MirrorCS", {"start": v(0.5, 5.33) * mm, "end": v(0.5, 2.54) * mm});
            skLineSegment(sketch, "E241.MirrorCS", {"start": v(0.5, 2.54) * mm, "end": v(0, 2.54) * mm});
            skSolve(sketch);
        }
        {
            var Q0;
            Q0 = qSketchRegion(id + "F20", true);
            extrude(context, id + "F21", {"entities" : qUnion([Q0]), "operationType" : NewBodyOperationType.REMOVE, "oppositeDirection" : true, "depth" : 6.35 * mm, "offsetDistance" : 25.4 * mm});
        }
        {
            var Q0;
            Q0 = qSketchRegion(id + "F17", true);
            var Q1;
            Q1=sQuery(id+"F17.wireOp",EDGE,"E206");
            revolve(context, id + "F22", {"operationType" : NewBodyOperationType.ADD, "surfaceOperationType" : NewSurfaceOperationType.NEW, "entities" : qUnion([Q0]), "axis" : qUnion([Q1]), "revolveType" : RevolveType.FULL});
        }
        {
            var Q0;
            Q0=qCreatedBy(makeId("Front.planeOp"),FACE);
            var sketch = newSketch(context, id + "F23", { "sketchPlane" : qUnion([Q0])});
            skLineSegment(sketch, "E242", {"start": v(0, 18.54) * mm, "end": v(-1.65, 18.54) * mm});
            skLineSegment(sketch, "E243", {"start": v(-1.65, 18.54) * mm, "end": v(-1.65, 17.78) * mm});
            skLineSegment(sketch, "E244", {"start": v(-1.65, 17.78) * mm, "end": v(0, 17.78) * mm});
            skLineSegment(sketch, "E245", {"start": v(0, 17.78) * mm, "end": v(0, 18.54) * mm});
            skSolve(sketch);
        }
        {
            var Q0;
            Q0 = qSketchRegion(id + "F23", true);
            var Q1;
            Q1=sQuery(id+"F23.wireOp",EDGE,"E245");
            revolve(context, id + "F24", {"operationType" : NewBodyOperationType.ADD, "surfaceOperationType" : NewSurfaceOperationType.NEW, "entities" : qUnion([Q0]), "axis" : qUnion([Q1]), "revolveType" : RevolveType.FULL});
        }
        {
            var Q0;
            Q0=makeQuery(id+"F24.opRevolve","SWEPT_EDGE",EDGE,{"disambiguationData":[OSD([sQuery(id+"F23.wireOp",EDGE,"E242"),sQuery(id+"F23.wireOp",EDGE,"E243")])]});
            var Q1;
            Q1=makeQuery(id+"F24.opRevolve","SWEPT_EDGE",EDGE,{"disambiguationData":[OSD([sQuery(id+"F23.wireOp",EDGE,"E243"),sQuery(id+"F23.wireOp",EDGE,"E244")])]});
            fillet(context, id + "F25", {"entities" : qUnion([Q0, Q1]), "radius" : 0.38 * mm, "tangentPropagation" : true, "allowEdgeOverflow" : false});
        }
        {
            var Q0;
            Q0=makeQuery(id+"F10.opRevolve","SWEPT_EDGE",EDGE,{"disambiguationData":[OSD([sQuery(id+"F9.wireOp",EDGE,"E180"),sQuery(id+"F9.wireOp",EDGE,"E181")])]});
            var Q1;
            {var subQ0=sQuery(id+"F23.wireOp",EDGE,"E244");Q1=makeQuery(id+"F25.opFillet","BLEND_EDGE",EDGE,{"blendedFrom":[makeQuery(id+"F24.opRevolve","SWEPT_EDGE",EDGE,{"disambiguationData":[OSD([sQuery(id+"F23.wireOp",EDGE,"E243"),subQ0])]}),makeQuery(id+"F24.boolean.opBoolean","SPLIT",FACE,{"disambiguationData":[TD([makeQuery(id+"F10.opRevolve","SWEPT_FACE",FACE,{"disambiguationData":[OSD([sQuery(id+"F9.wireOp",EDGE,"E183")])]})])],"derivedFrom":makeQuery(id+"F10.opRevolve","SWEPT_FACE",FACE,{"disambiguationData":[OSD([sQuery(id+"F9.wireOp",EDGE,"E180")])]})})],"blendedInto":[makeQuery(id+"F24.boolean.opBoolean","SPLIT",FACE,{"disambiguationData":[TD([makeQuery(id+"F10.opRevolve","SWEPT_FACE",FACE,{"disambiguationData":[OSD([sQuery(id+"F9.wireOp",EDGE,"E183")])]})])],"derivedFrom":makeQuery(id+"F10.opRevolve","SWEPT_FACE",FACE,{"disambiguationData":[OSD([sQuery(id+"F9.wireOp",EDGE,"E180")])]})})]});}
            var Q2;
            {var subQ0=sQuery(id+"F23.wireOp",EDGE,"E242");Q2=makeQuery(id+"F25.opFillet","BLEND_EDGE",EDGE,{"blendedFrom":[makeQuery(id+"F24.opRevolve","SWEPT_EDGE",EDGE,{"disambiguationData":[OSD([subQ0,sQuery(id+"F23.wireOp",EDGE,"E243")])]}),makeQuery(id+"F24.boolean.opBoolean","SPLIT",FACE,{"disambiguationData":[TD([makeQuery(id+"F10.opRevolve","SWEPT_FACE",FACE,{"disambiguationData":[OSD([sQuery(id+"F9.wireOp",EDGE,"E181")])]})])],"derivedFrom":makeQuery(id+"F10.opRevolve","SWEPT_FACE",FACE,{"disambiguationData":[OSD([sQuery(id+"F9.wireOp",EDGE,"E180")])]})})],"blendedInto":[makeQuery(id+"F24.boolean.opBoolean","SPLIT",FACE,{"disambiguationData":[TD([makeQuery(id+"F10.opRevolve","SWEPT_FACE",FACE,{"disambiguationData":[OSD([sQuery(id+"F9.wireOp",EDGE,"E181")])]})])],"derivedFrom":makeQuery(id+"F10.opRevolve","SWEPT_FACE",FACE,{"disambiguationData":[OSD([sQuery(id+"F9.wireOp",EDGE,"E180")])]})})]});}
            fillet(context, id + "F26", {"entities" : qUnion([Q0, Q1, Q2]), "radius" : 0.25 * mm, "tangentPropagation" : true, "allowEdgeOverflow" : false});
        }
    });
